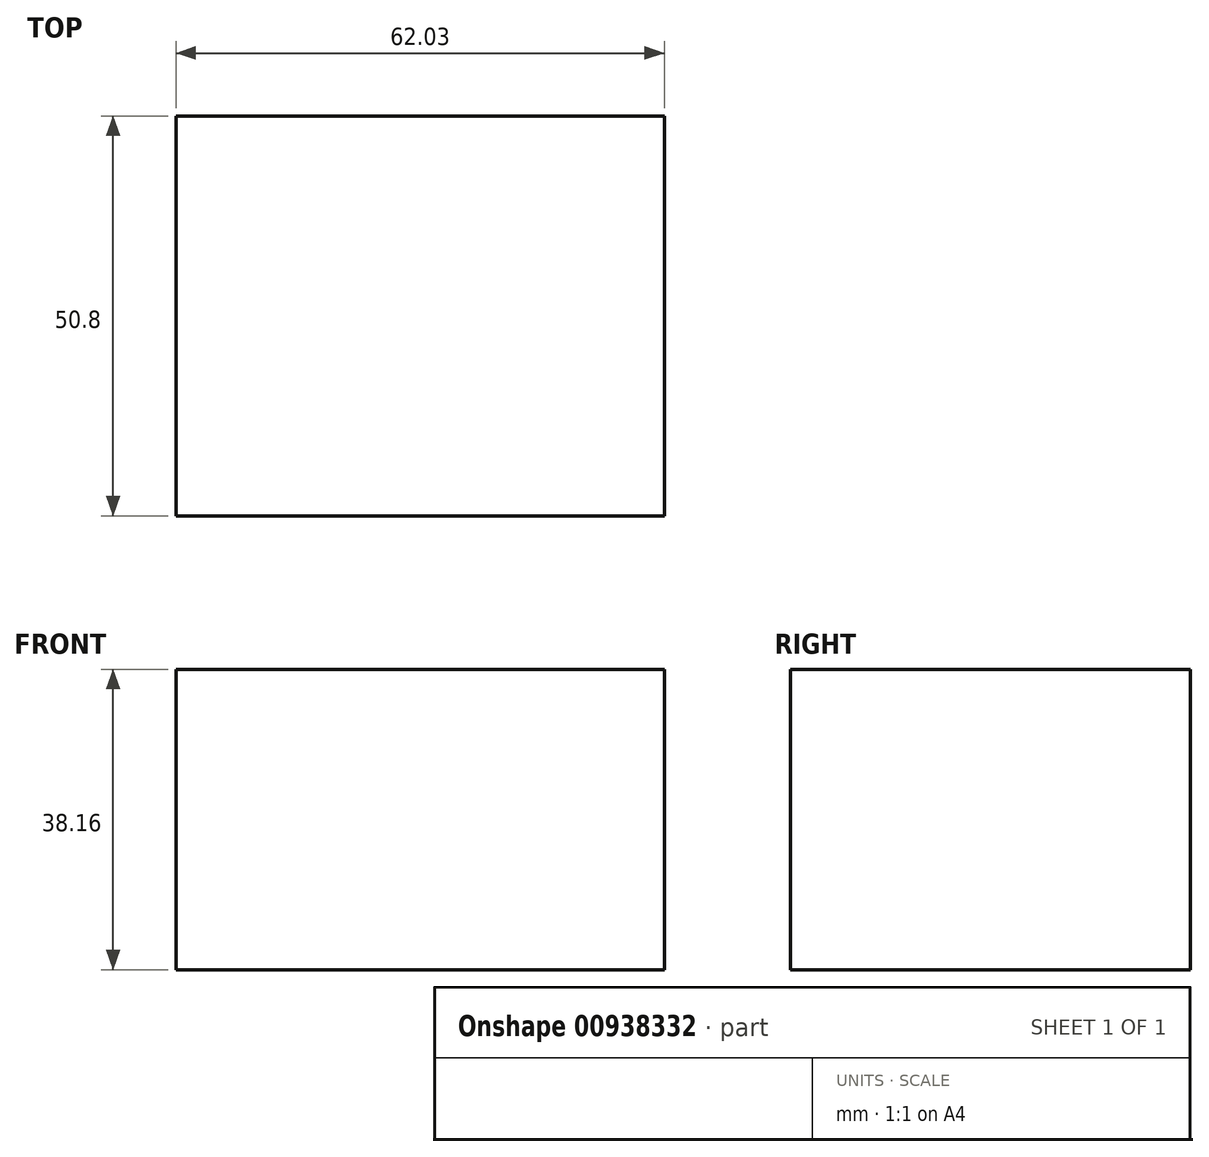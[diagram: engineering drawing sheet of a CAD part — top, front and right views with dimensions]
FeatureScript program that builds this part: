
annotation { "Feature Type Name" : "Feature", "Feature Type Description" : "" }
export const myFeature = defineFeature(function(context is Context, id is Id, definition is map)
    precondition{}
    {
        {
            var Q0;
            Q0=qCreatedBy(makeId("Front.planeOp"),FACE);
            var sketch = newSketch(context, id + "F0", { "sketchPlane" : qUnion([Q0])});
            skLineSegment(sketch, "E0", {"start": v(0, 0) * mm, "end": v(62.03, 0) * mm});
            skLineSegment(sketch, "E1", {"start": v(62.03, 0) * mm, "end": v(62.03, 38.16) * mm});
            skLineSegment(sketch, "E2", {"start": v(62.03, 38.16) * mm, "end": v(0, 38.16) * mm});
            skLineSegment(sketch, "E3", {"start": v(0, 38.16) * mm, "end": v(0, 0) * mm});
            skSolve(sketch);
        }
        {
            var Q0;
            Q0=makeQuery(id+"F0.imprint","IMPRINT",FACE,{"disambiguationData":[TD([[makeQuery(id+"F0.imprint","IMPRINT",EDGE,{"derivedFrom":sQuery(id+"F0.wireOp",EDGE,"E0")}),1.0]])]});
            extrude(context, id + "F1", {"entities" : qUnion([Q0]), "oppositeDirection" : true, "depth" : 50.8 * mm, "offsetDistance" : 25.4 * mm});
        }
    });
